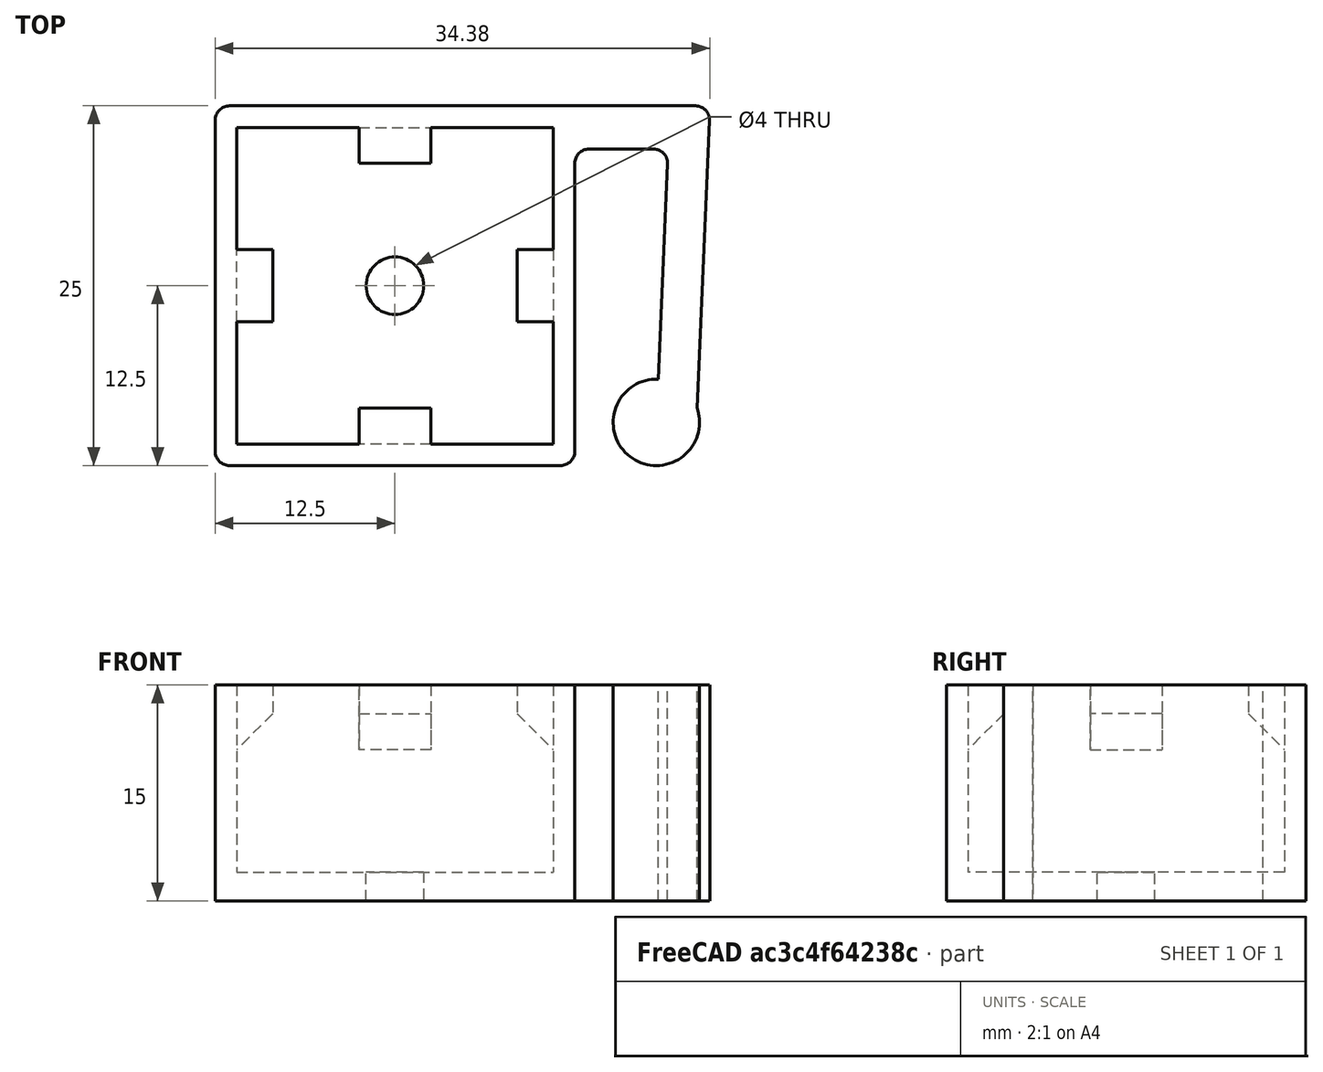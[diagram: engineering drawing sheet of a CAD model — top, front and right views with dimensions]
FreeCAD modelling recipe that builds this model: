
FCSTD DOCUMENT  (FreeCAD 0.18R16146 (Git))
Label: clip
License: All rights reserved
LicenseURL: http://en.wikipedia.org/wiki/All_rights_reserved
objects: PartDesign::Mirrored×7, Sketcher::SketchObject×5, PartDesign::Fillet×4, PartDesign::Pad×3, PartDesign::Plane×3, PartDesign::Pocket×2, PartDesign::Body×1, Mesh::Feature×1
note: 30 computed .brp shape members not serialized (recipe doc carries the construction recipe); baked Part::Feature solids carry a one-line shape summary decoded from their .brp

FEATURE [Sketcher::SketchObject] Sketch
  MapMode = 5
  Support = -> [XY_Plane]
  sketch-geometry (10):
    g0: LineSegment StartX=0 StartY=0 StartZ=0 EndX=25 EndY=0 EndZ=0
    g1: LineSegment StartX=25 StartY=0 StartZ=0 EndX=25 EndY=22 EndZ=0
    g2: LineSegment StartX=25 StartY=22 StartZ=0 EndX=31.5 EndY=22 EndZ=0
    g3: LineSegment StartX=31.5 StartY=22 StartZ=0 EndX=30.7981 EndY=5.99712 EndZ=0
    g4: ArcOfCircle CenterX=30.6667 CenterY=3 CenterZ=0 NormalX=0 NormalY=0 NormalZ=1 AngleXU=0 Radius=3 StartAngle=1.52696 EndAngle=6.28319
    g5: ArcOfCircle CenterX=30.6667 CenterY=3 CenterZ=0 NormalX=0 NormalY=0 NormalZ=1 AngleXU=0 Radius=3 StartAngle=0 EndAngle=0.334896
    g6: LineSegment StartX=33.5 StartY=3.98601 StartZ=0 EndX=34.4217 EndY=25 EndZ=0
    g7: LineSegment StartX=34.4217 StartY=25 StartZ=0 EndX=25 EndY=25 EndZ=0
    g8: LineSegment StartX=25 StartY=25 StartZ=0 EndX=0 EndY=25 EndZ=0
    g9: LineSegment StartX=0 StartY=25 StartZ=0 EndX=0 EndY=0 EndZ=0
  constraints (29):
    c: Horizontal(g0)
    c: Coincident(g0,g1)
    c: Vertical(g1)
    c: Coincident(g1,g2)
    c: Horizontal(g2)
    c: Coincident(g2,g3)
    c: Perpendicular(g3,g4) = 4.71239
    c: Tangent(g4,g5) = -1.5708
    c: Coincident(g5,g6)
    c: Coincident(g6,g7)
    c: Horizontal(g7)
    c: Coincident(g7,g8)
    c: Horizontal(g8)
    c: Coincident(g8,g9)
    c: Coincident(g9,g0)
    c: Vertical(g9)
    c: Radius(g5) = 3
    c: Radius(g4) = 3
    c: Tangent(g5,g-1)
    c: Coincident(g0,g-1)
    c: Equal(g8,g9)
    c: Equal(g9,g0)
    c: Parallel(g6,g3)
    c: DistanceY(g1,g7) = 3
    c: DistanceY(g9,g9) = 25
    c: DistanceX(g2,g2) = 6.5
    c: Distance(g4,g5) = 1
    c: DistanceY(g4) = 3
    c: DistanceX(g5) = 33.5
FEATURE [PartDesign::Pad] Pad
  Length = 15
  Length2 = 100
  Profile = -> Sketch
  Refine = true
  Type = 0
FEATURE [Sketcher::SketchObject] Sketch001
  ExternalGeometry = -> [Pad]
  MapMode = 5
  Placement = pos=(0,0,15) rot=(0,0,1;0rad)
  Support = -> [Pad]
  sketch-geometry (1):
    g0: Circle CenterX=12.5 CenterY=12.5 CenterZ=0 NormalX=0 NormalY=0 NormalZ=1 AngleXU=0 Radius=2
  constraints (2):
    c: Symmetric(g-3,g-4,g0)
    c: Diameter(g0) = 4
FEATURE [PartDesign::Pocket] Pocket
  BaseFeature = -> Pad
  Length = 5
  Length2 = 100
  Profile = -> Sketch001
  Refine = true
  Type = 1
FEATURE [Sketcher::SketchObject] Sketch002
  ExternalGeometry = -> [Pocket]
  MapMode = 5
  Placement = pos=(0,0,15) rot=(0,0,1;0rad)
  Support = -> [Pocket]
  sketch-geometry (5):
    g0: LineSegment StartX=1.5 StartY=23.5 StartZ=0 EndX=23.5 EndY=23.5 EndZ=0
    g1: LineSegment StartX=23.5 StartY=23.5 StartZ=0 EndX=23.5 EndY=1.5 EndZ=0
    g2: LineSegment StartX=23.5 StartY=1.5 StartZ=0 EndX=1.5 EndY=1.5 EndZ=0
    g3: LineSegment StartX=1.5 StartY=1.5 StartZ=0 EndX=1.5 EndY=23.5 EndZ=0
    g4: GeomPoint X=12.5 Y=12.5 Z=0
  constraints (12):
    c: Coincident(g0,g1)
    c: Coincident(g1,g2)
    c: Coincident(g2,g3)
    c: Coincident(g3,g0)
    c: Horizontal(g0)
    c: Horizontal(g2)
    c: Vertical(g1)
    c: Vertical(g3)
    c: Equal(g0,g3)
    c: DistanceX(g0,g0) = 22
    c: Symmetric(g0,g1,g4)
    c: Symmetric(g-3,g-5,g4)
FEATURE [PartDesign::Pocket] Pocket001
  BaseFeature = -> Pocket
  Length = 13
  Length2 = 100
  Profile = -> Sketch002
  Refine = true
  Type = 0
FEATURE [Sketcher::SketchObject] Sketch003
  ExternalGeometry = -> [Pocket001]
  MapMode = 5
  Placement = pos=(0,0,15) rot=(0,0,1;0rad)
  Support = -> [Pocket001]
  sketch-geometry (5):
    g0: LineSegment StartX=1.5 StartY=15 StartZ=0 EndX=4 EndY=15 EndZ=0
    g1: LineSegment StartX=4 StartY=15 StartZ=0 EndX=4 EndY=10 EndZ=0
    g2: LineSegment StartX=4 StartY=10 StartZ=0 EndX=1.5 EndY=10 EndZ=0
    g3: LineSegment StartX=1.5 StartY=10 StartZ=0 EndX=1.5 EndY=15 EndZ=0
    g4: GeomPoint X=1.5 Y=12.5 Z=0
  constraints (12):
    c: Coincident(g0,g1)
    c: Coincident(g1,g2)
    c: Coincident(g2,g3)
    c: Coincident(g3,g0)
    c: Horizontal(g0)
    c: Horizontal(g2)
    c: Vertical(g1)
    c: Vertical(g3)
    c: Symmetric(g0,g2,g4)
    c: DistanceX(g2,g2) = 2.5
    c: DistanceY(g1,g1) = 5
    c: Symmetric(g-4,g-5,g4)
FEATURE [PartDesign::Pad] Pad001
  BaseFeature = -> Pocket001
  Length = 2
  Length2 = 100
  Profile = -> Sketch003
  Refine = true
  Reversed = true
  Type = 0
FEATURE [Sketcher::SketchObject] Sketch004
  ExternalGeometry = -> [Pad001]
  MapMode = 5
  Placement = pos=(0,10,0) rot=(1,0,0;1.5708rad)
  Support = -> [Pad001]
  sketch-geometry (3):
    g0: LineSegment StartX=4 StartY=13 StartZ=0 EndX=1.5 EndY=10.5 EndZ=0
    g1: LineSegment StartX=1.5 StartY=10.5 StartZ=0 EndX=1.5 EndY=13 EndZ=0
    g2: LineSegment StartX=1.5 StartY=13 StartZ=0 EndX=4 EndY=13 EndZ=0
  constraints (8):
    c: Coincident(g-4,g0)
    c: PointOnObject(g0,g-3)
    c: Coincident(g0,g1)
    c: PointOnObject(g1,g-3)
    c: Coincident(g1,g2)
    c: Coincident(g2,g0)
    c: Horizontal(g2)
    c: Angle(g0,g1) = 0.785398
FEATURE [PartDesign::Pad] Pad002
  BaseFeature = -> Pad001
  Length = 5
  Length2 = 100
  Profile = -> Sketch004
  Refine = true
  Reversed = true
  Type = 0
FEATURE [PartDesign::Plane] DatumPlane
  AttachmentOffset = pos=(0,-6,11) rot=(0,0,1;0rad)
  Length = 40.9161
  MapMode = 5
  Placement = pos=(12.5,0,-6) rot=(0.57735,-0.57735,-0.57735;2.0944rad)
  ResizeMode = 0
  Support = -> [Pad002]
  Width = 30.9161
FEATURE [PartDesign::Mirrored] Mirrored
  BaseFeature = -> Pad002
  MirrorPlane = -> DatumPlane
  Originals = -> [Pad001]
  Refine = true
FEATURE [PartDesign::Mirrored] Mirrored001
  BaseFeature = -> Mirrored
  MirrorPlane = -> DatumPlane
  Originals = -> [Pad002]
  Refine = true
FEATURE [PartDesign::Fillet] Fillet
  Base = -> Mirrored001 [Edge8]
  BaseFeature = -> Mirrored001
  Radius = 1
FEATURE [PartDesign::Fillet] Fillet001
  Base = -> Fillet [Edge38]
  BaseFeature = -> Fillet
  Radius = 1
FEATURE [PartDesign::Fillet] Fillet002
  Base = -> Fillet001 [Edge31]
  BaseFeature = -> Fillet001
  Radius = 1
FEATURE [PartDesign::Fillet] Fillet003
  Base = -> Fillet002 [Edge28,Edge24,Edge22]
  BaseFeature = -> Fillet002
  Radius = 1
FEATURE [PartDesign::Plane] DatumPlane001
  AttachmentOffset = pos=(0,0,0) rot=(0,1,0;0.785398rad)
  Length = 63.619
  MapMode = 3
  Placement = pos=(0,0,0) rot=(0.862856,0.357407,0.357407;1.71777rad)
  ResizeMode = 0
  Support = -> [Fillet003]
  Width = 32.4918
FEATURE [PartDesign::Mirrored] Mirrored002
  BaseFeature = -> Fillet003
  MirrorPlane = -> DatumPlane001
  Originals = -> [Pad002]
  Refine = true
FEATURE [PartDesign::Mirrored] Mirrored003
  BaseFeature = -> Mirrored002
  MirrorPlane = -> DatumPlane001
  Originals = -> [Pad002]
  Refine = true
FEATURE [PartDesign::Mirrored] Mirrored004
  BaseFeature = -> Mirrored003
  MirrorPlane = -> DatumPlane001
  Originals = -> [Pad001]
  Refine = true
FEATURE [PartDesign::Plane] DatumPlane002
  AttachmentOffset = pos=(0,0,-25) rot=(0,-1,0;0.785398rad)
  Length = 63.619
  MapMode = 3
  Placement = pos=(0,25,-5.6e-15) rot=(0.862856,-0.357407,-0.357407;1.71777rad)
  ResizeMode = 0
  Support = -> [Pad001]
  Width = 32.4918
FEATURE [PartDesign::Mirrored] Mirrored005
  BaseFeature = -> Mirrored004
  MirrorPlane = -> DatumPlane002
  Originals = -> [Pad001]
  Refine = true
FEATURE [PartDesign::Mirrored] Mirrored006
  BaseFeature = -> Mirrored005
  MirrorPlane = -> DatumPlane002
  Originals = -> [Pad002]
  Refine = true
FEATURE [PartDesign::Body] Body
  Group = -> [Sketch,Pad,Sketch001,Pocket,Sketch002,Pocket001,Sketch003,Pad001,Sketch004,Pad002,DatumPlane,Mirrored,Mirrored001,Fillet,Fillet001,Fillet002,Fillet003,DatumPlane001,Mirrored002,Mirrored003,Mirrored004,DatumPlane002,Mirrored005,Mirrored006]
  Origin = -> Origin
  Tip = -> Mirrored006
FEATURE [Mesh::Feature] Mesh  label="Body (Meshed)"
